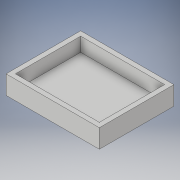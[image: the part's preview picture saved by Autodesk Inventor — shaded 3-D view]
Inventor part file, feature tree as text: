
AUTODESK INVENTOR PART (.ipt)
format: ipt  version: 2019 (Build 230136000, 136)  size: 108,544 bytes
history: native  units: mm
features: extrude x2, sketch x2, projected_geometry x1
ambient origin geometry x8: Origin, YZ Plane, XZ Plane, XY Plane, X Axis, Y Axis, Z Axis, Center Point
bodies: Volumenkörper1 (feature_tree)
feature tree (5):
  extrude  "Extrusion1"  Depth=80.0mm
  extrude  "Extrusion2"  Depth=90.0mm
  sketch  "Skizze1"  dims[d0=100.0mm d1=80.0mm]
  sketch  "Skizze2"  dims[d2=5.0mm d3=0.0mm d4=90.0mm d5=70.0mm d6=15.0mm d7=0.0mm]
  projected_geometry  "Projizierte Kontur1"
